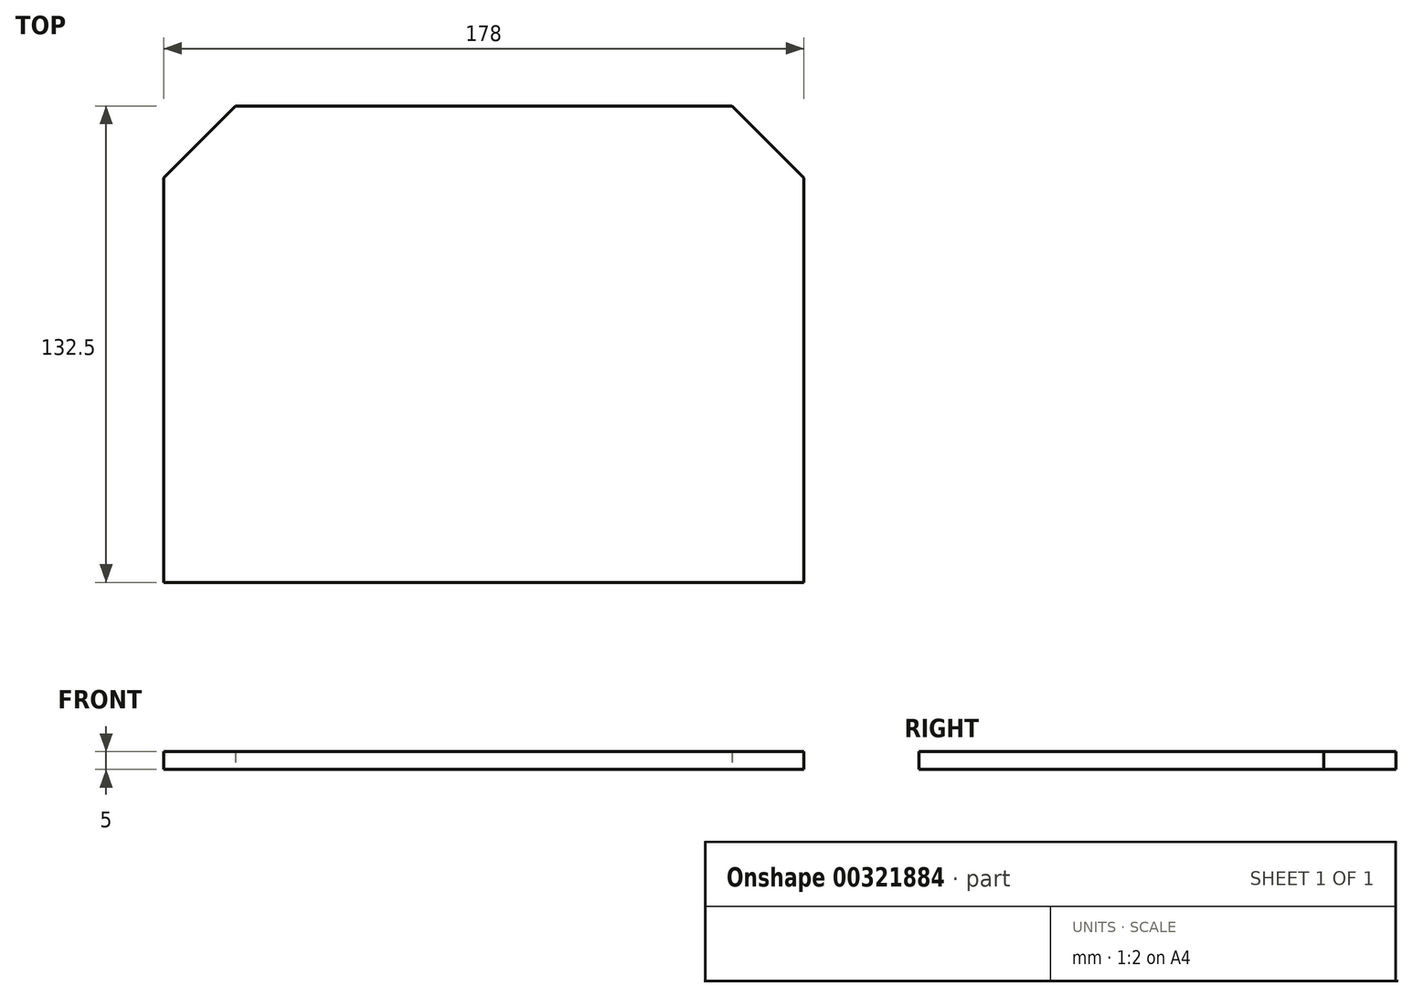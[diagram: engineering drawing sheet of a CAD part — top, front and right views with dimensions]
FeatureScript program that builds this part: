
annotation { "Feature Type Name" : "Feature", "Feature Type Description" : "" }
export const myFeature = defineFeature(function(context is Context, id is Id, definition is map)
    precondition{}
    {
        {
            var Q0;
            Q0=qCreatedBy(makeId("Top.planeOp"),FACE);
            var sketch = newSketch(context, id + "F0", { "sketchPlane" : qUnion([Q0])});
            skLineSegment(sketch, "E0.top", {"start": v(-158, -14.45) * mm, "end": v(20, -14.45) * mm});
            skLineSegment(sketch, "E1", {"start": v(20, -14.45) * mm, "end": v(20, 98.05) * mm});
            skLineSegment(sketch, "E2", {"start": v(0, 118.05) * mm, "end": v(20, 98.05) * mm});
            skLineSegment(sketch, "E3", {"start": v(-158, -14.45) * mm, "end": v(-158, 98.05) * mm});
            skLineSegment(sketch, "E4", {"start": v(-138, 118.05) * mm, "end": v(-158, 98.05) * mm});
            skLineSegment(sketch, "E5", {"start": v(-138, 118.05) * mm, "end": v(0, 118.05) * mm});
            skSolve(sketch);
        }
        {
            var Q0;
            Q0=makeQuery(id+"F0.imprint","IMPRINT",FACE,{"disambiguationData":[TD([[makeQuery(id+"F0.imprint","IMPRINT",EDGE,{"derivedFrom":sQuery(id+"F0.wireOp",EDGE,"E0.top")}),1.0]])]});
            extrude(context, id + "F1", {"entities" : qUnion([Q0]), "depth" : 5 * mm});
        }
    });
